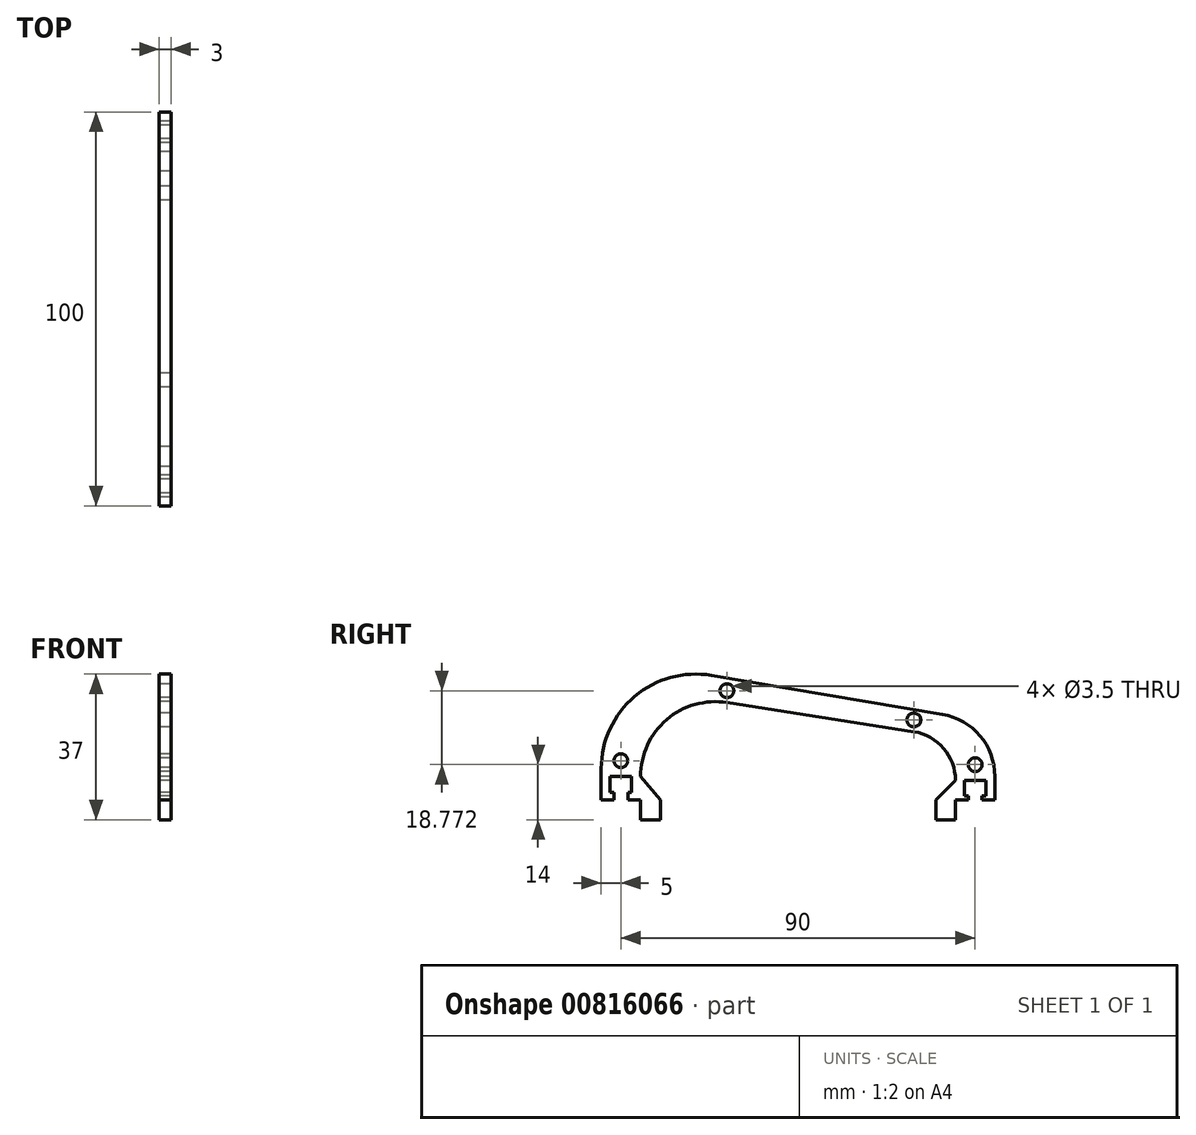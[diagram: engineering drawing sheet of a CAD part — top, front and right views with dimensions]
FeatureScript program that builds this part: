
annotation { "Feature Type Name" : "Feature", "Feature Type Description" : "" }
export const myFeature = defineFeature(function(context is Context, id is Id, definition is map)
    precondition{}
    {
        {
            var Q0;
            Q0=qCreatedBy(makeId("Top.planeOp"),FACE);
            var sketch = newSketch(context, id + "F0", { "sketchPlane" : qUnion([Q0])});
            skLineSegment(sketch, "E0.bottom", {"start": v(20, 20) * mm, "end": v(-20, 20) * mm, "construction": true});
            skLineSegment(sketch, "E0.top", {"start": v(20, -20) * mm, "end": v(-20, -20) * mm, "construction": true});
            skLineSegment(sketch, "E0.left", {"start": v(20, 20) * mm, "end": v(20, -20) * mm, "construction": true});
            skLineSegment(sketch, "E0.right", {"start": v(-20, 20) * mm, "end": v(-20, -20) * mm, "construction": true});
            skPoint(sketch, "E0.middle", {"position": v(0, 0) * mm});
            skSolve(sketch);
        }
        {
            var Q0;
            Q0=qCreatedBy(makeId("Right.planeOp"),FACE);
            var sketch = newSketch(context, id + "F1", { "sketchPlane" : qUnion([Q0])});
            skLineSegment(sketch, "E1", {"start": v(-50, 0) * mm, "end": v(-50, 8) * mm});
            skArc(sketch, "E2", {"start": v(-50, 8) * mm, "mid": v(-41.5, 26.33) * mm, "end": v(-22.01, 31.67) * mm});
            skLineSegment(sketch, "E3", {"start": v(-22.01, 31.67) * mm, "end": v(36.66, 21.78) * mm});
            skLineSegment(sketch, "E4", {"start": v(50, 0) * mm, "end": v(50, 6) * mm});
            skArc(sketch, "E5", {"start": v(50, 6) * mm, "mid": v(46.22, 16.33) * mm, "end": v(36.66, 21.78) * mm});
            skArc(sketch, "E6", {"start": v(-40, 6) * mm, "mid": v(-33.35, 20.43) * mm, "end": v(-18.07, 24.77) * mm});
            skArc(sketch, "E7", {"start": v(40, 5) * mm, "mid": v(37, 13.13) * mm, "end": v(29.43, 17.35) * mm});
            skLineSegment(sketch, "E8", {"start": v(-18.07, 24.77) * mm, "end": v(29.43, 17.35) * mm});
            skLineSegment(sketch, "E9", {"start": v(5.68, 21.06) * mm, "end": v(6.57, 26.72) * mm, "construction": true});
            skPoint(sketch, "E9.endSnap0", {"position": v(7.32, 26.72) * mm});
            skLineSegment(sketch, "E10", {"start": v(-47.75, 6) * mm, "end": v(-42.25, 6) * mm});
            skLineSegment(sketch, "E11", {"start": v(-42.25, 6) * mm, "end": v(-42.25, 2) * mm});
            skLineSegment(sketch, "E12", {"start": v(-47.75, 6) * mm, "end": v(-47.75, 2) * mm});
            skLineSegment(sketch, "E13", {"start": v(-47.75, 2) * mm, "end": v(-46.75, 2) * mm});
            skLineSegment(sketch, "E14", {"start": v(-42.25, 2) * mm, "end": v(-43.25, 2) * mm});
            skLineSegment(sketch, "E15", {"start": v(-43.25, 2) * mm, "end": v(-43.25, 0) * mm});
            skLineSegment(sketch, "E16", {"start": v(-43.25, 0) * mm, "end": v(-40, 0) * mm});
            skLineSegment(sketch, "E17", {"start": v(-46.75, 2) * mm, "end": v(-46.75, 0) * mm});
            skLineSegment(sketch, "E18", {"start": v(-46.75, 0) * mm, "end": v(-50, 0) * mm});
            skLineSegment(sketch, "E19", {"start": v(40, 0) * mm, "end": v(43.25, 0) * mm});
            skLineSegment(sketch, "E20", {"start": v(43.25, 0) * mm, "end": v(43.25, 1) * mm});
            skLineSegment(sketch, "E21", {"start": v(43.25, 1) * mm, "end": v(42.25, 1) * mm});
            skLineSegment(sketch, "E22", {"start": v(42.25, 1) * mm, "end": v(42.25, 5) * mm});
            skLineSegment(sketch, "E23", {"start": v(42.25, 5) * mm, "end": v(47.75, 5) * mm});
            skLineSegment(sketch, "E24", {"start": v(47.75, 5) * mm, "end": v(47.75, 1) * mm});
            skLineSegment(sketch, "E25", {"start": v(47.75, 1) * mm, "end": v(46.75, 1) * mm});
            skLineSegment(sketch, "E26", {"start": v(46.75, 1) * mm, "end": v(46.75, 0) * mm});
            skLineSegment(sketch, "E27", {"start": v(46.75, 0) * mm, "end": v(50, 0) * mm});
            skCircle(sketch, "E28", {"center": v(-18.07, 27.77) * mm, "radius": 1.75 * mm});
            skCircle(sketch, "E29", {"center": v(29.43, 20.35) * mm, "radius": 1.75 * mm});
            skPoint(sketch, "E30.centerSnap0", {"position": v(-45, 6) * mm});
            skCircle(sketch, "E31", {"center": v(-45, 10) * mm, "radius": 1.75 * mm});
            skCircle(sketch, "E32", {"center": v(45, 9) * mm, "radius": 1.75 * mm});
            skPoint(sketch, "E32.centerSnap0", {"position": v(45, 5) * mm});
            skLineSegment(sketch, "E33", {"start": v(-40, 6) * mm, "end": v(-35, 0) * mm});
            skLineSegment(sketch, "E34", {"start": v(-35, 0) * mm, "end": v(-35, -5) * mm});
            skLineSegment(sketch, "E35", {"start": v(-35, -5) * mm, "end": v(-40, -5) * mm});
            skLineSegment(sketch, "E36", {"start": v(-40, -5) * mm, "end": v(-40, 0) * mm});
            skLineSegment(sketch, "E37", {"start": v(40, 5) * mm, "end": v(35, 0) * mm});
            skLineSegment(sketch, "E38", {"start": v(35, 0) * mm, "end": v(35, -5) * mm});
            skLineSegment(sketch, "E39", {"start": v(35, -5) * mm, "end": v(40, -5) * mm});
            skLineSegment(sketch, "E40", {"start": v(40, -5) * mm, "end": v(40, 0) * mm});
            skSolve(sketch);
        }
        {
            var Q0;
            Q0=makeQuery(id+"F1.imprint","IMPRINT",FACE,{"disambiguationData":[TD([[makeQuery(id+"F1.imprint","IMPRINT",EDGE,{"derivedFrom":sQuery(id+"F1.wireOp",EDGE,"E1")}),-1.0]])]});
            extrude(context, id + "F2", {"entities" : qUnion([Q0]), "depth" : 3 * mm, "offsetDistance" : 25 * mm});
        }
    });
